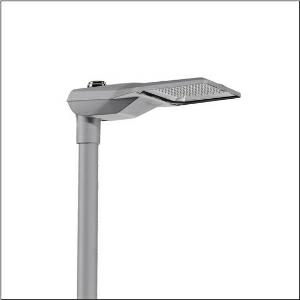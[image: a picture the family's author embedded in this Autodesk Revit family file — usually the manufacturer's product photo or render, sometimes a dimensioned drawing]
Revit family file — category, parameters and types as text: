
# Revit family: streetlight_sl_21_midi___st0_8a_5xe7c37n08nb_761f
name_source: partatom
category: Lighting Fixtures
units: mm (PartAtom-declared; Revit-internal decimal feet)

## family parameters
Cut with Voids When Loaded = No
Host = Face
Light Source = No
Part Type = Normal
Room Calculation Point = No
Round Connector Dimension = Use Diameter
Shared = No

## types (1)
- --- (1 x LED, 22700 lm, 151.2 W, 3000K)
    Apparent Load = 151 VA
    CIE Flux Codes = 41 75 97 100 100
    Color Rendering = 70
    Color Temperature = 3000K
    Default Elevation = 1800 mm
    Description = Streetlight SL 21 midi, mast luminaire, primary light control with lens, of PMMA, primary optical cover: cover, of toughened safety glass, transparent, light distribution: ST0.8a, light emission: direct distribution, primary light characteristic: asymmetric, installation type: side-entry, LED, 3G 2.5mm², High Power LED, rated luminous flux: 22.700lm, luminous efficacy: 150lm/W, light colour: 730, colour temperature: 3000K, control gear: NEMA (7pin), control: overheat protection, pre-setting: linear dimming characteristic, constant luminous flux control, time-dependent luminous flux control, flexible luminous flux parameterisation, mains connection: 220..240V, AC, 50/60Hz, connection cable pre-assembled, cable length: 12,5m, wiring characteristics: H05VV-F, start of lifetime: 151W, end of service life: 157W, reduction: 70W, luminaire housing, of diecast aluminium (EN AC-44300), powder-coated, SITECO metallic grey (DB 702S), corrosivity category C5 high according to DIN EN ISO 12944, multi-level sealing system, sealing non-destructively replaceable, inclination adjustable: 0°, 5°, 10°, 15°, length: 644mm, width: 335mm, height: 110mm, spigot size: 42mm (side-entry), mounting height: 4..8m, protection rating (complete): IP66, insulation class (complete): insulation class I (protective earthing), certification: CE, ENEC, ENEC+, VDE, impact resistance: IK10, permissible operating ambient temperature for outdoor applications: -40..+50°C, standard-compliant lighting for roads and squares, packaging unit: 1 piece

Light Distribution: ST0.8a
    Height = 111 mm
    Lamp = 1 x LED
    Lamp Light Flux = 22700 lm
    Lamp Power = 151.2 W
    Lamp count = 1
    Length = 644 mm
    Luminous efficacy = 150 lm/W
    Manufacturer = Siteco
    ModVariant = No
    Model = 5XE7C37N08NB
    Number of Poles = 1
    OnlyDefault = Yes
    Power Factor = 1
    Product Name = Streetlight SL 21 midi | ST0.8a
    Product group = mast luminaire | pylon top
    ProductGroupID = 6100
    Protection Class = Protection class I
    Protection Degree = IP 66
    RLX_Detail_Level = 1
    RLX_Emergency_Light_Flux = 0 lm
    RLX_Emergency_Type = 0
    RLX_Emergency_Type_DB = No
    RlxData = <blob elided: 26585 chars, md5=2fea346c>
    Socket = socket
    Standby Power = 0 W
    System Light Flux = 22700 lm
    System Power = 151 W
    Type Comments = factory setting: luminous flux: 100 % | dim-lin: 254 | 802 mA
    Type Image = l_1294377.jpg
    URL = http://relux.com
    VarID = @adj_133369
    Voltage = 0 V
    Weight = 0.00 kg
    Width = 336 mm

## geometry (parser evidence)
native form markers: Blend x4, Sweep x11
no freeform markers — native parametric forms only
